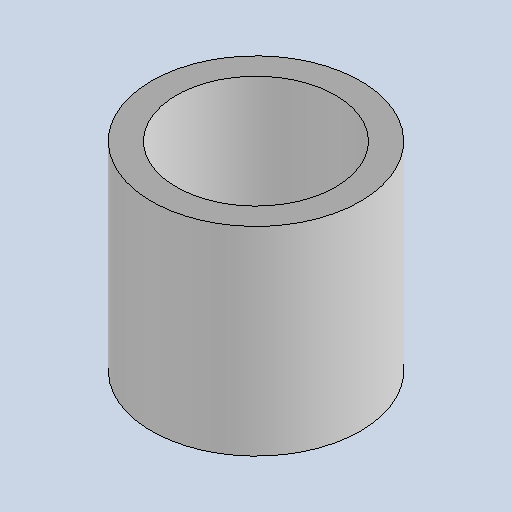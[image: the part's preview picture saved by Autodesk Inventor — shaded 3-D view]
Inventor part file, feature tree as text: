
AUTODESK INVENTOR PART (.ipt)
format: ipt  version: 2025.1 (Build 291241020, 241B)  size: 89,088 bytes
history: native  units: mm
features: extrude x1, sketch x1
ambient origin geometry x8: Origin, YZ Plane, XZ Plane, XY Plane, X Axis, Y Axis, Z Axis, Center Point
bodies: Solid1 (feature_tree)
feature tree (2):
  extrude  "Extrusion1"  Depth=20.0mm
  sketch  "Sketch1"  dims[d0=21.0mm d1=16.0mm d2=20.0mm d3=0.0mm]
